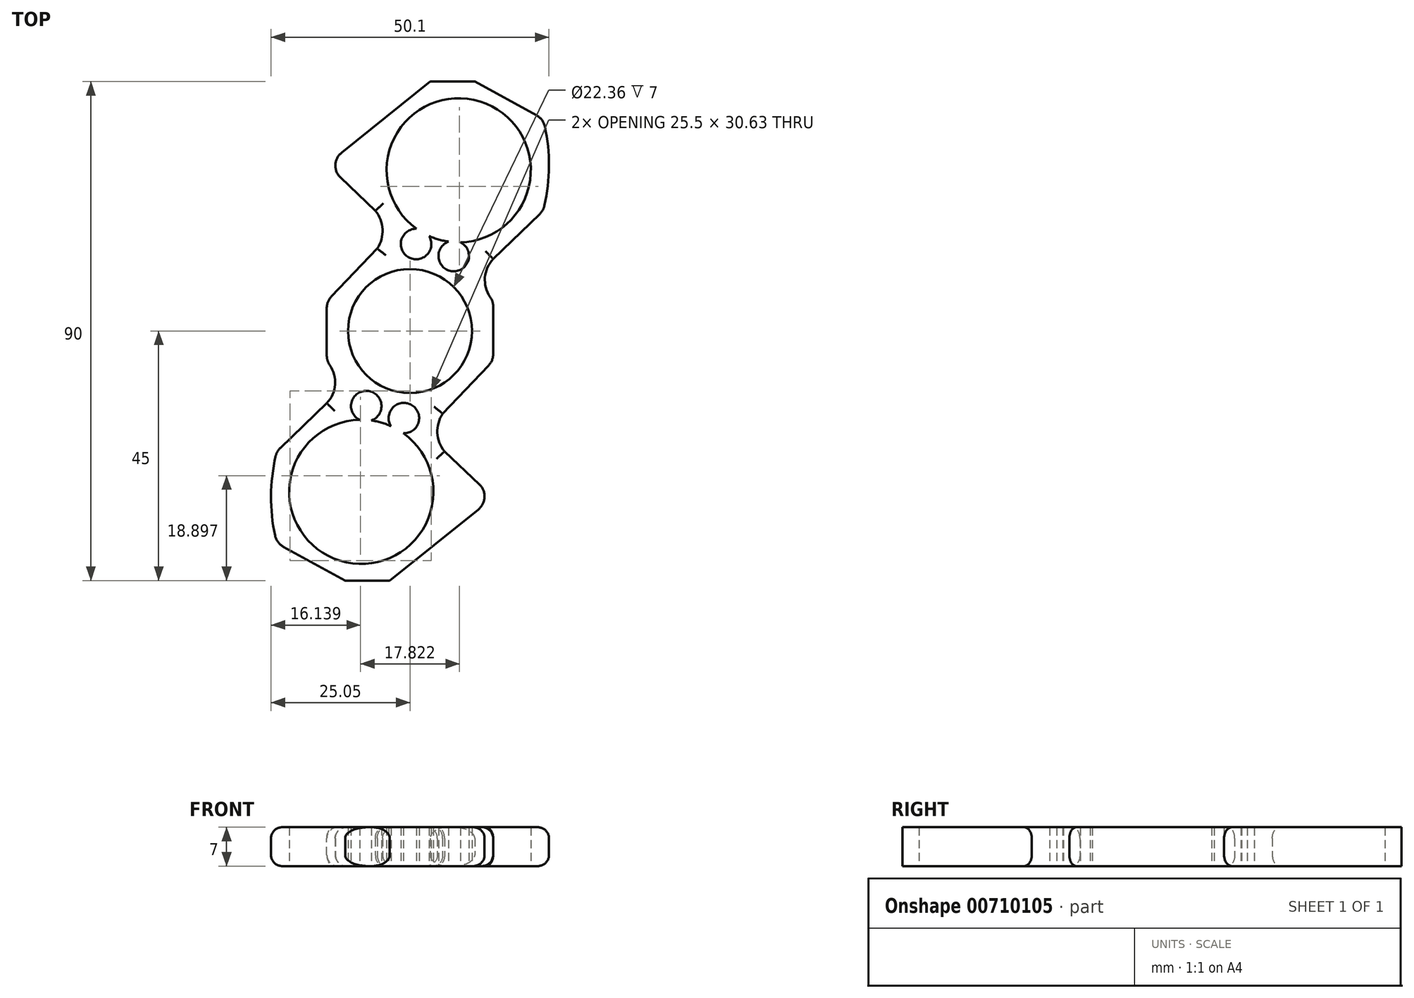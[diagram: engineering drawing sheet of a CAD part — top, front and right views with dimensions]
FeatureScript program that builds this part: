
annotation { "Feature Type Name" : "Feature", "Feature Type Description" : "" }
export const myFeature = defineFeature(function(context is Context, id is Id, definition is map)
    precondition{}
    {
        {
            var Q0;
            Q0=qCreatedBy(makeId("Top.planeOp"),FACE);
            var sketch = newSketch(context, id + "F0", { "sketchPlane" : qUnion([Q0])});
            skLineSegment(sketch, "E0.bottom", {"start": v(11.7, 45) * mm, "end": v(3.66, 45) * mm});
            skLineSegment(sketch, "E0.top", {"start": v(-3.66, -45) * mm, "end": v(-11.7, -45) * mm});
            skLineSegment(sketch, "E0.left", {"start": v(15, 43.2) * mm, "end": v(15, 13) * mm});
            skLineSegment(sketch, "E0.right", {"start": v(-15, 5.33) * mm, "end": v(-15, -43.2) * mm});
            skPoint(sketch, "E0.middle", {"position": v(0, 0) * mm});
            skCircle(sketch, "E1", {"center": v(0, 0) * mm, "radius": 11.18 * mm});
            skCircle(sketch, "E2", {"center": v(0, 0) * mm, "radius": 13 * mm});
            skLineSegment(sketch, "E3.right", {"start": v(24, 38.27) * mm, "end": v(24, 21.7) * mm});
            skLineSegment(sketch, "E4.left", {"start": v(-15, -45) * mm, "end": v(-15, -13) * mm});
            skLineSegment(sketch, "E4.right", {"start": v(-24, -38.27) * mm, "end": v(-24, -21.7) * mm});
            skPoint(sketch, "E5", {"position": v(-15, -29) * mm});
            skPoint(sketch, "E6", {"position": v(-8.78, -29) * mm});
            skCircle(sketch, "E7", {"center": v(-8.78, -29) * mm, "radius": 11.18 * mm});
            skCircle(sketch, "E8", {"center": v(-8.78, -29) * mm, "radius": 13 * mm});
            skCircle(sketch, "E9.1.0", {"center": v(8.78, 29) * mm, "radius": 11.18 * mm});
            skCircle(sketch, "E9.1.1", {"center": v(8.78, 29) * mm, "radius": 13 * mm});
            skLineSegment(sketch, "E10", {"start": v(-15, 5.33) * mm, "end": v(-5.35, 15.48) * mm});
            skLineSegment(sketch, "E11", {"start": v(-5.35, 15.48) * mm, "end": v(-2.67, 18.3) * mm});
            skLineSegment(sketch, "E12", {"start": v(-2.67, 18.3) * mm, "end": v(-15, 30.03) * mm});
            skLineSegment(sketch, "E13", {"start": v(-15, 30.03) * mm, "end": v(3.66, 45) * mm});
            skLineSegment(sketch, "E14", {"start": v(3.66, 45) * mm, "end": v(11.7, 45) * mm});
            skLineSegment(sketch, "E15", {"start": v(11.7, 45) * mm, "end": v(24, 38.27) * mm});
            skLineSegment(sketch, "E16", {"start": v(24, 21.7) * mm, "end": v(15, 13) * mm});
            skPoint(sketch, "E17.orphan", {"position": v(-15, 45) * mm});
            skPoint(sketch, "E18.orphan", {"position": v(24, 45) * mm});
            skPoint(sketch, "E19.orphan", {"position": v(15, 45) * mm});
            skPoint(sketch, "E20.orphan", {"position": v(24, 13) * mm});
            skLineSegment(sketch, "E21", {"start": v(15, 5.48) * mm, "end": v(10.3, 10.42) * mm});
            skLineSegment(sketch, "E22", {"start": v(10.3, 10.42) * mm, "end": v(15, 13) * mm});
            skLineSegment(sketch, "E23.trimOffspring", {"start": v(15, 5.48) * mm, "end": v(15, -5.33) * mm});
            skArc(sketch, "E24", {"start": v(11.7, 45) * mm, "mid": v(7.68, 46.41) * mm, "end": v(3.66, 45) * mm});
            skArc(sketch, "E25", {"start": v(24, 21.7) * mm, "mid": v(25.05, 29.98) * mm, "end": v(24, 38.27) * mm});
            skArc(sketch, "E26", {"start": v(-5.9, 14.9) * mm, "mid": v(-4.94, 18.35) * mm, "end": v(-6.24, 21.7) * mm});
            skArc(sketch, "E27", {"start": v(15, 13) * mm, "mid": v(13.5, 9.24) * mm, "end": v(15, 5.48) * mm});
            skLineSegment(sketch, "E28.1.0", {"start": v(15, -30.03) * mm, "end": v(-3.66, -45) * mm});
            skLineSegment(sketch, "E28.1.1", {"start": v(2.67, -18.3) * mm, "end": v(15, -30.03) * mm});
            skArc(sketch, "E28.1.2", {"start": v(5.9, -14.9) * mm, "mid": v(4.94, -18.35) * mm, "end": v(6.24, -21.7) * mm});
            skLineSegment(sketch, "E28.1.3", {"start": v(5.35, -15.48) * mm, "end": v(2.67, -18.3) * mm});
            skLineSegment(sketch, "E28.1.4", {"start": v(15, -5.33) * mm, "end": v(5.35, -15.48) * mm});
            skArc(sketch, "E28.1.5", {"start": v(-15, -13) * mm, "mid": v(-13.5, -9.24) * mm, "end": v(-15, -5.48) * mm});
            skLineSegment(sketch, "E28.1.6", {"start": v(-10.3, -10.42) * mm, "end": v(-15, -13) * mm});
            skLineSegment(sketch, "E28.1.7", {"start": v(-15, -5.48) * mm, "end": v(-10.3, -10.42) * mm});
            skLineSegment(sketch, "E28.1.8", {"start": v(-24, -21.7) * mm, "end": v(-15, -13) * mm});
            skArc(sketch, "E28.1.10", {"start": v(-24, -21.7) * mm, "mid": v(-25.05, -29.98) * mm, "end": v(-24, -38.27) * mm});
            skLineSegment(sketch, "E28.1.11", {"start": v(-11.7, -45) * mm, "end": v(-24, -38.27) * mm});
            skArc(sketch, "E28.1.13", {"start": v(-11.7, -45) * mm, "mid": v(-7.68, -46.41) * mm, "end": v(-3.66, -45) * mm});
            skPoint(sketch, "E29.orphan", {"position": v(-24, -13) * mm});
            skPoint(sketch, "E30.orphan", {"position": v(-24, -45) * mm});
            skPoint(sketch, "E31.orphan", {"position": v(15, -45) * mm});
            skSolve(sketch);
        }
        {
            var Q0;
            Q0=makeQuery(id+"F0.imprint","IMPRINT",FACE,{"disambiguationData":[TD([[makeQuery(id+"F0.imprint","IMPRINT",EDGE,{"derivedFrom":sQuery(id+"F0.wireOp",EDGE,"E2")}),-1.0]])]});
            var Q1;
            {var subQ0=sQuery(id+"F0.wireOp",EDGE,"E28.1.8");Q1=makeQuery(id+"F0.imprint","IMPRINT",FACE,{"disambiguationData":[TD([[makeQuery(id+"F0.imprint","IMPRINT",EDGE,{"derivedFrom":subQ0}),-1.0]])]});}
            var Q2;
            Q2=makeQuery(id+"F0.imprint","IMPRINT",FACE,{"disambiguationData":[TD([[makeQuery(id+"F0.imprint","IMPRINT",EDGE,{"derivedFrom":sQuery(id+"F0.wireOp",EDGE,"E4.right")}),1.0]])]});
            var Q3;
            Q3=makeQuery(id+"F0.imprint","IMPRINT",FACE,{"disambiguationData":[TD([[makeQuery(id+"F0.imprint","IMPRINT",EDGE,{"derivedFrom":sQuery(id+"F0.wireOp",EDGE,"E0.top")}),1.0]])]});
            var Q4;
            {var subQ0=sQuery(id+"F0.wireOp",EDGE,"E8");var subQ1=sQuery(id+"F0.wireOp",EDGE,"E4.left");var subQ2=makeQuery(id+"F0.imprint","INTERSECT",VERTEX,{"disambiguationData":[OD(0.0)],"derivedFrom":[subQ1,subQ0]});Q4=makeQuery(id+"F0.imprint","IMPRINT",FACE,{"disambiguationData":[TD([[makeQuery(id+"F0.imprint","IMPRINT",EDGE,{"disambiguationData":[TD([[subQ2,-1.0]])],"derivedFrom":subQ1}),-1.0]])]});}
            var Q5;
            {var subQ0=sQuery(id+"F0.wireOp",EDGE,"E8");var subQ1=sQuery(id+"F0.wireOp",EDGE,"E4.left");var subQ2=makeQuery(id+"F0.imprint","INTERSECT",VERTEX,{"disambiguationData":[OD(0.0)],"derivedFrom":[subQ1,subQ0]});Q5=makeQuery(id+"F0.imprint","IMPRINT",FACE,{"disambiguationData":[TD([[makeQuery(id+"F0.imprint","IMPRINT",EDGE,{"disambiguationData":[TD([[subQ2,-1.0]])],"derivedFrom":subQ1}),1.0]])]});}
            var Q6;
            Q6=makeQuery(id+"F0.imprint","IMPRINT",FACE,{"disambiguationData":[TD([[makeQuery(id+"F0.imprint","IMPRINT",EDGE,{"derivedFrom":sQuery(id+"F0.wireOp",EDGE,"E1")}),-1.0]])]});
            var Q7;
            {var subQ0=sQuery(id+"F0.wireOp",EDGE,"E9.1.1");var subQ1=sQuery(id+"F0.wireOp",EDGE,"E0.left");var subQ2=makeQuery(id+"F0.imprint","INTERSECT",VERTEX,{"disambiguationData":[OD(0.0)],"derivedFrom":[subQ1,subQ0]});Q7=makeQuery(id+"F0.imprint","IMPRINT",FACE,{"disambiguationData":[TD([[makeQuery(id+"F0.imprint","IMPRINT",EDGE,{"disambiguationData":[TD([[subQ2,-1.0]])],"derivedFrom":subQ1}),1.0]])]});}
            var Q8;
            {var subQ0=sQuery(id+"F0.wireOp",EDGE,"E9.1.1");var subQ1=sQuery(id+"F0.wireOp",EDGE,"E0.left");var subQ2=makeQuery(id+"F0.imprint","INTERSECT",VERTEX,{"disambiguationData":[OD(0.0)],"derivedFrom":[subQ1,subQ0]});Q8=makeQuery(id+"F0.imprint","IMPRINT",FACE,{"disambiguationData":[TD([[makeQuery(id+"F0.imprint","IMPRINT",EDGE,{"disambiguationData":[TD([[subQ2,-1.0]])],"derivedFrom":subQ1}),-1.0]])]});}
            var Q9;
            Q9=makeQuery(id+"F0.imprint","IMPRINT",FACE,{"disambiguationData":[TD([[makeQuery(id+"F0.imprint","IMPRINT",EDGE,{"derivedFrom":sQuery(id+"F0.wireOp",EDGE,"E3.right")}),1.0]])]});
            var Q10;
            {var subQ3=sQuery(id+"F0.wireOp",EDGE,"E3.right");Q10=makeQuery(id+"F0.imprint","IMPRINT",FACE,{"disambiguationData":[TD([[makeQuery(id+"F0.imprint","IMPRINT",EDGE,{"derivedFrom":subQ3}),-1.0]])]});}
            var Q11;
            Q11=makeQuery(id+"F0.imprint","IMPRINT",FACE,{"disambiguationData":[TD([[makeQuery(id+"F0.imprint","IMPRINT",EDGE,{"derivedFrom":sQuery(id+"F0.wireOp",EDGE,"E14")}),1.0]])]});
            var Q12;
            {var subQ2=sQuery(id+"F0.wireOp",EDGE,"E28.1.2");Q12=makeQuery(id+"F0.imprint","IMPRINT",FACE,{"disambiguationData":[TD([[makeQuery(id+"F0.imprint","IMPRINT",EDGE,{"derivedFrom":subQ2}),-1.0]])]});}
            var Q13;
            {var subQ0=sQuery(id+"F0.wireOp",EDGE,"E11");Q13=makeQuery(id+"F0.imprint","IMPRINT",FACE,{"disambiguationData":[TD([[makeQuery(id+"F0.imprint","IMPRINT",EDGE,{"derivedFrom":subQ0}),1.0]])]});}
            var Q14;
            Q14=makeQuery(id+"F0.imprint","IMPRINT",FACE,{"disambiguationData":[TD([[makeQuery(id+"F0.imprint","IMPRINT",EDGE,{"derivedFrom":sQuery(id+"F0.wireOp",EDGE,"E28.1.5")}),-1.0]])]});
            var Q15;
            Q15=makeQuery(id+"F0.imprint","IMPRINT",FACE,{"disambiguationData":[TD([[makeQuery(id+"F0.imprint","IMPRINT",EDGE,{"derivedFrom":sQuery(id+"F0.wireOp",EDGE,"E21")}),-1.0]])]});
            extrude(context, id + "F1", {"entities" : qUnion([Q0, Q1, Q2, Q3, Q4, Q5, Q6, Q7, Q8, Q9, Q10, Q11, Q12, Q13, Q14, Q15]), "depth" : 7 * mm, "offsetDistance" : 25 * mm});
        }
        {
            var Q0;
            Q0=makeQuery(id+"F1.opExtrude","SWEPT_EDGE",EDGE,{"disambiguationData":[OSD([sQuery(id+"F0.wireOp",EDGE,"E28.1.0"),sQuery(id+"F0.wireOp",EDGE,"E28.1.1")])]});
            var Q1;
            Q1=makeQuery(id+"F1.opExtrude","SWEPT_EDGE",EDGE,{"disambiguationData":[OSD([sQuery(id+"F0.wireOp",EDGE,"E12"),sQuery(id+"F0.wireOp",EDGE,"E13")])]});
            var Q2;
            Q2=makeQuery(id+"F1.opExtrude","SWEPT_EDGE",EDGE,{"disambiguationData":[OSD([sQuery(id+"F0.wireOp",EDGE,"E15"),sQuery(id+"F0.wireOp",EDGE,"E3.right"),sQuery(id+"F0.wireOp",EDGE,"E25")])]});
            var Q3;
            Q3=makeQuery(id+"F1.opExtrude","SWEPT_EDGE",EDGE,{"disambiguationData":[OSD([sQuery(id+"F0.wireOp",EDGE,"E3.right"),sQuery(id+"F0.wireOp",EDGE,"E16"),sQuery(id+"F0.wireOp",EDGE,"E25")])]});
            var Q4;
            Q4=makeQuery(id+"F1.opExtrude","SWEPT_EDGE",EDGE,{"disambiguationData":[OSD([sQuery(id+"F0.wireOp",EDGE,"E21"),sQuery(id+"F0.wireOp",EDGE,"E23.trimOffspring"),sQuery(id+"F0.wireOp",EDGE,"E27")])]});
            var Q5;
            Q5=makeQuery(id+"F1.opExtrude","SWEPT_EDGE",EDGE,{"disambiguationData":[OSD([sQuery(id+"F0.wireOp",EDGE,"E23.trimOffspring"),sQuery(id+"F0.wireOp",EDGE,"E28.1.4")])]});
            var Q6;
            Q6=makeQuery(id+"F1.opExtrude","SWEPT_EDGE",EDGE,{"disambiguationData":[OSD([sQuery(id+"F0.wireOp",EDGE,"E4.right"),sQuery(id+"F0.wireOp",EDGE,"E28.1.10"),sQuery(id+"F0.wireOp",EDGE,"E28.1.11")])]});
            var Q7;
            Q7=makeQuery(id+"F1.opExtrude","SWEPT_EDGE",EDGE,{"disambiguationData":[OSD([sQuery(id+"F0.wireOp",EDGE,"E28.1.8"),sQuery(id+"F0.wireOp",EDGE,"E4.right"),sQuery(id+"F0.wireOp",EDGE,"E28.1.10")])]});
            var Q8;
            Q8=makeQuery(id+"F1.opExtrude","SWEPT_EDGE",EDGE,{"disambiguationData":[OSD([sQuery(id+"F0.wireOp",EDGE,"E0.right"),sQuery(id+"F0.wireOp",EDGE,"E28.1.5"),sQuery(id+"F0.wireOp",EDGE,"E28.1.7")])]});
            var Q9;
            Q9=makeQuery(id+"F1.opExtrude","SWEPT_EDGE",EDGE,{"disambiguationData":[OSD([sQuery(id+"F0.wireOp",EDGE,"E0.right"),sQuery(id+"F0.wireOp",EDGE,"E10")])]});
            fillet(context, id + "F2", {"entities" : qUnion([Q0, Q1, Q2, Q3, Q4, Q5, Q6, Q7, Q8, Q9]), "radius" : 3 * mm, "tangentPropagation" : true, "allowEdgeOverflow" : false});
        }
        {
            var Q0;
            Q0=makeQuery(id+"F1.opExtrude","CAP_EDGE",EDGE,{"disambiguationData":[OSD([sQuery(id+"F0.wireOp",EDGE,"E23.trimOffspring")])],"isStart":true});
            var Q1;
            {var subQ0=sQuery(id+"F0.wireOp",EDGE,"E28.1.4");var subQ1=sQuery(id+"F0.wireOp",EDGE,"E23.trimOffspring");Q1=makeQuery(id+"F2.opFillet","BLEND_EDGE",EDGE,{"blendedFrom":[makeQuery(id+"F1.opExtrude","SWEPT_EDGE",EDGE,{"disambiguationData":[OSD([subQ1,subQ0])]}),makeQuery(id+"F1.opExtrude","CAP_FACE",FACE,{"disambiguationData":[OSD([sQuery(id+"F0.wireOp",EDGE,"E0.right"),sQuery(id+"F0.wireOp",EDGE,"E1"),sQuery(id+"F0.wireOp",EDGE,"E7"),sQuery(id+"F0.wireOp",EDGE,"E9.1.0"),sQuery(id+"F0.wireOp",EDGE,"E10"),sQuery(id+"F0.wireOp",EDGE,"E12"),sQuery(id+"F0.wireOp",EDGE,"E13"),sQuery(id+"F0.wireOp",EDGE,"E15"),sQuery(id+"F0.wireOp",EDGE,"E16"),subQ1,sQuery(id+"F0.wireOp",EDGE,"E24"),sQuery(id+"F0.wireOp",EDGE,"E25"),sQuery(id+"F0.wireOp",EDGE,"E26"),sQuery(id+"F0.wireOp",EDGE,"E27"),sQuery(id+"F0.wireOp",EDGE,"E28.1.0"),sQuery(id+"F0.wireOp",EDGE,"E28.1.1"),sQuery(id+"F0.wireOp",EDGE,"E28.1.2"),subQ0,sQuery(id+"F0.wireOp",EDGE,"E28.1.5"),sQuery(id+"F0.wireOp",EDGE,"E28.1.8"),sQuery(id+"F0.wireOp",EDGE,"E28.1.10"),sQuery(id+"F0.wireOp",EDGE,"E28.1.11"),sQuery(id+"F0.wireOp",EDGE,"E28.1.13")])],"isStart":true})],"blendedInto":[makeQuery(id+"F1.opExtrude","CAP_FACE",FACE,{"disambiguationData":[OSD([sQuery(id+"F0.wireOp",EDGE,"E0.right"),sQuery(id+"F0.wireOp",EDGE,"E1"),sQuery(id+"F0.wireOp",EDGE,"E7"),sQuery(id+"F0.wireOp",EDGE,"E9.1.0"),sQuery(id+"F0.wireOp",EDGE,"E10"),sQuery(id+"F0.wireOp",EDGE,"E12"),sQuery(id+"F0.wireOp",EDGE,"E13"),sQuery(id+"F0.wireOp",EDGE,"E15"),sQuery(id+"F0.wireOp",EDGE,"E16"),subQ1,sQuery(id+"F0.wireOp",EDGE,"E24"),sQuery(id+"F0.wireOp",EDGE,"E25"),sQuery(id+"F0.wireOp",EDGE,"E26"),sQuery(id+"F0.wireOp",EDGE,"E27"),sQuery(id+"F0.wireOp",EDGE,"E28.1.0"),sQuery(id+"F0.wireOp",EDGE,"E28.1.1"),sQuery(id+"F0.wireOp",EDGE,"E28.1.2"),subQ0,sQuery(id+"F0.wireOp",EDGE,"E28.1.5"),sQuery(id+"F0.wireOp",EDGE,"E28.1.8"),sQuery(id+"F0.wireOp",EDGE,"E28.1.10"),sQuery(id+"F0.wireOp",EDGE,"E28.1.11"),sQuery(id+"F0.wireOp",EDGE,"E28.1.13")])],"isStart":true})]});}
            var Q2;
            Q2=makeQuery(id+"F1.opExtrude","CAP_EDGE",EDGE,{"disambiguationData":[OSD([sQuery(id+"F0.wireOp",EDGE,"E28.1.4")])],"isStart":true});
            var Q3;
            Q3=makeQuery(id+"F1.opExtrude","CAP_EDGE",EDGE,{"disambiguationData":[OSD([sQuery(id+"F0.wireOp",EDGE,"E28.1.2")])],"isStart":true});
            var Q4;
            Q4=makeQuery(id+"F1.opExtrude","CAP_EDGE",EDGE,{"disambiguationData":[OSD([sQuery(id+"F0.wireOp",EDGE,"E28.1.1")])],"isStart":true});
            var Q5;
            {var subQ0=sQuery(id+"F0.wireOp",EDGE,"E28.1.1");var subQ1=sQuery(id+"F0.wireOp",EDGE,"E28.1.0");Q5=makeQuery(id+"F2.opFillet","BLEND_EDGE",EDGE,{"blendedFrom":[makeQuery(id+"F1.opExtrude","SWEPT_EDGE",EDGE,{"disambiguationData":[OSD([subQ1,subQ0])]}),makeQuery(id+"F1.opExtrude","CAP_FACE",FACE,{"disambiguationData":[OSD([sQuery(id+"F0.wireOp",EDGE,"E0.right"),sQuery(id+"F0.wireOp",EDGE,"E1"),sQuery(id+"F0.wireOp",EDGE,"E7"),sQuery(id+"F0.wireOp",EDGE,"E9.1.0"),sQuery(id+"F0.wireOp",EDGE,"E10"),sQuery(id+"F0.wireOp",EDGE,"E12"),sQuery(id+"F0.wireOp",EDGE,"E13"),sQuery(id+"F0.wireOp",EDGE,"E15"),sQuery(id+"F0.wireOp",EDGE,"E16"),sQuery(id+"F0.wireOp",EDGE,"E23.trimOffspring"),sQuery(id+"F0.wireOp",EDGE,"E24"),sQuery(id+"F0.wireOp",EDGE,"E25"),sQuery(id+"F0.wireOp",EDGE,"E26"),sQuery(id+"F0.wireOp",EDGE,"E27"),subQ1,subQ0,sQuery(id+"F0.wireOp",EDGE,"E28.1.2"),sQuery(id+"F0.wireOp",EDGE,"E28.1.4"),sQuery(id+"F0.wireOp",EDGE,"E28.1.5"),sQuery(id+"F0.wireOp",EDGE,"E28.1.8"),sQuery(id+"F0.wireOp",EDGE,"E28.1.10"),sQuery(id+"F0.wireOp",EDGE,"E28.1.11"),sQuery(id+"F0.wireOp",EDGE,"E28.1.13")])],"isStart":true})],"blendedInto":[makeQuery(id+"F1.opExtrude","CAP_FACE",FACE,{"disambiguationData":[OSD([sQuery(id+"F0.wireOp",EDGE,"E0.right"),sQuery(id+"F0.wireOp",EDGE,"E1"),sQuery(id+"F0.wireOp",EDGE,"E7"),sQuery(id+"F0.wireOp",EDGE,"E9.1.0"),sQuery(id+"F0.wireOp",EDGE,"E10"),sQuery(id+"F0.wireOp",EDGE,"E12"),sQuery(id+"F0.wireOp",EDGE,"E13"),sQuery(id+"F0.wireOp",EDGE,"E15"),sQuery(id+"F0.wireOp",EDGE,"E16"),sQuery(id+"F0.wireOp",EDGE,"E23.trimOffspring"),sQuery(id+"F0.wireOp",EDGE,"E24"),sQuery(id+"F0.wireOp",EDGE,"E25"),sQuery(id+"F0.wireOp",EDGE,"E26"),sQuery(id+"F0.wireOp",EDGE,"E27"),subQ1,subQ0,sQuery(id+"F0.wireOp",EDGE,"E28.1.2"),sQuery(id+"F0.wireOp",EDGE,"E28.1.4"),sQuery(id+"F0.wireOp",EDGE,"E28.1.5"),sQuery(id+"F0.wireOp",EDGE,"E28.1.8"),sQuery(id+"F0.wireOp",EDGE,"E28.1.10"),sQuery(id+"F0.wireOp",EDGE,"E28.1.11"),sQuery(id+"F0.wireOp",EDGE,"E28.1.13")])],"isStart":true})]});}
            var Q6;
            Q6=makeQuery(id+"F1.opExtrude","CAP_EDGE",EDGE,{"disambiguationData":[OSD([sQuery(id+"F0.wireOp",EDGE,"E28.1.0")])],"isStart":true});
            var Q7;
            Q7=makeQuery(id+"F1.opExtrude","CAP_EDGE",EDGE,{"disambiguationData":[OSD([sQuery(id+"F0.wireOp",EDGE,"E28.1.13")])],"isStart":true});
            var Q8;
            Q8=makeQuery(id+"F1.opExtrude","CAP_EDGE",EDGE,{"disambiguationData":[OSD([sQuery(id+"F0.wireOp",EDGE,"E28.1.11")])],"isStart":true});
            var Q9;
            Q9=makeQuery(id+"F1.opExtrude","CAP_EDGE",EDGE,{"disambiguationData":[OSD([sQuery(id+"F0.wireOp",EDGE,"E0.right")])],"isStart":true});
            var Q10;
            {var subQ0=sQuery(id+"F0.wireOp",EDGE,"E10");var subQ1=sQuery(id+"F0.wireOp",EDGE,"E0.right");Q10=makeQuery(id+"F2.opFillet","BLEND_EDGE",EDGE,{"blendedFrom":[makeQuery(id+"F1.opExtrude","SWEPT_EDGE",EDGE,{"disambiguationData":[OSD([subQ1,subQ0])]}),makeQuery(id+"F1.opExtrude","CAP_FACE",FACE,{"disambiguationData":[OSD([subQ1,sQuery(id+"F0.wireOp",EDGE,"E1"),sQuery(id+"F0.wireOp",EDGE,"E7"),sQuery(id+"F0.wireOp",EDGE,"E9.1.0"),subQ0,sQuery(id+"F0.wireOp",EDGE,"E12"),sQuery(id+"F0.wireOp",EDGE,"E13"),sQuery(id+"F0.wireOp",EDGE,"E15"),sQuery(id+"F0.wireOp",EDGE,"E16"),sQuery(id+"F0.wireOp",EDGE,"E23.trimOffspring"),sQuery(id+"F0.wireOp",EDGE,"E24"),sQuery(id+"F0.wireOp",EDGE,"E25"),sQuery(id+"F0.wireOp",EDGE,"E26"),sQuery(id+"F0.wireOp",EDGE,"E27"),sQuery(id+"F0.wireOp",EDGE,"E28.1.0"),sQuery(id+"F0.wireOp",EDGE,"E28.1.1"),sQuery(id+"F0.wireOp",EDGE,"E28.1.2"),sQuery(id+"F0.wireOp",EDGE,"E28.1.4"),sQuery(id+"F0.wireOp",EDGE,"E28.1.5"),sQuery(id+"F0.wireOp",EDGE,"E28.1.8"),sQuery(id+"F0.wireOp",EDGE,"E28.1.10"),sQuery(id+"F0.wireOp",EDGE,"E28.1.11"),sQuery(id+"F0.wireOp",EDGE,"E28.1.13")])],"isStart":true})],"blendedInto":[makeQuery(id+"F1.opExtrude","CAP_FACE",FACE,{"disambiguationData":[OSD([subQ1,sQuery(id+"F0.wireOp",EDGE,"E1"),sQuery(id+"F0.wireOp",EDGE,"E7"),sQuery(id+"F0.wireOp",EDGE,"E9.1.0"),subQ0,sQuery(id+"F0.wireOp",EDGE,"E12"),sQuery(id+"F0.wireOp",EDGE,"E13"),sQuery(id+"F0.wireOp",EDGE,"E15"),sQuery(id+"F0.wireOp",EDGE,"E16"),sQuery(id+"F0.wireOp",EDGE,"E23.trimOffspring"),sQuery(id+"F0.wireOp",EDGE,"E24"),sQuery(id+"F0.wireOp",EDGE,"E25"),sQuery(id+"F0.wireOp",EDGE,"E26"),sQuery(id+"F0.wireOp",EDGE,"E27"),sQuery(id+"F0.wireOp",EDGE,"E28.1.0"),sQuery(id+"F0.wireOp",EDGE,"E28.1.1"),sQuery(id+"F0.wireOp",EDGE,"E28.1.2"),sQuery(id+"F0.wireOp",EDGE,"E28.1.4"),sQuery(id+"F0.wireOp",EDGE,"E28.1.5"),sQuery(id+"F0.wireOp",EDGE,"E28.1.8"),sQuery(id+"F0.wireOp",EDGE,"E28.1.10"),sQuery(id+"F0.wireOp",EDGE,"E28.1.11"),sQuery(id+"F0.wireOp",EDGE,"E28.1.13")])],"isStart":true})]});}
            var Q11;
            Q11=makeQuery(id+"F1.opExtrude","CAP_EDGE",EDGE,{"disambiguationData":[OSD([sQuery(id+"F0.wireOp",EDGE,"E26")])],"isStart":true});
            var Q12;
            Q12=makeQuery(id+"F1.opExtrude","CAP_EDGE",EDGE,{"disambiguationData":[OSD([sQuery(id+"F0.wireOp",EDGE,"E12")])],"isStart":true});
            var Q13;
            Q13=makeQuery(id+"F1.opExtrude","CAP_EDGE",EDGE,{"disambiguationData":[OSD([sQuery(id+"F0.wireOp",EDGE,"E13")])],"isStart":true});
            var Q14;
            {var subQ0=sQuery(id+"F0.wireOp",EDGE,"E13");var subQ1=sQuery(id+"F0.wireOp",EDGE,"E12");Q14=makeQuery(id+"F2.opFillet","BLEND_EDGE",EDGE,{"blendedFrom":[makeQuery(id+"F1.opExtrude","SWEPT_EDGE",EDGE,{"disambiguationData":[OSD([subQ1,subQ0])]}),makeQuery(id+"F1.opExtrude","CAP_FACE",FACE,{"disambiguationData":[OSD([sQuery(id+"F0.wireOp",EDGE,"E0.right"),sQuery(id+"F0.wireOp",EDGE,"E1"),sQuery(id+"F0.wireOp",EDGE,"E7"),sQuery(id+"F0.wireOp",EDGE,"E9.1.0"),sQuery(id+"F0.wireOp",EDGE,"E10"),subQ1,subQ0,sQuery(id+"F0.wireOp",EDGE,"E15"),sQuery(id+"F0.wireOp",EDGE,"E16"),sQuery(id+"F0.wireOp",EDGE,"E23.trimOffspring"),sQuery(id+"F0.wireOp",EDGE,"E24"),sQuery(id+"F0.wireOp",EDGE,"E25"),sQuery(id+"F0.wireOp",EDGE,"E26"),sQuery(id+"F0.wireOp",EDGE,"E27"),sQuery(id+"F0.wireOp",EDGE,"E28.1.0"),sQuery(id+"F0.wireOp",EDGE,"E28.1.1"),sQuery(id+"F0.wireOp",EDGE,"E28.1.2"),sQuery(id+"F0.wireOp",EDGE,"E28.1.4"),sQuery(id+"F0.wireOp",EDGE,"E28.1.5"),sQuery(id+"F0.wireOp",EDGE,"E28.1.8"),sQuery(id+"F0.wireOp",EDGE,"E28.1.10"),sQuery(id+"F0.wireOp",EDGE,"E28.1.11"),sQuery(id+"F0.wireOp",EDGE,"E28.1.13")])],"isStart":true})],"blendedInto":[makeQuery(id+"F1.opExtrude","CAP_FACE",FACE,{"disambiguationData":[OSD([sQuery(id+"F0.wireOp",EDGE,"E0.right"),sQuery(id+"F0.wireOp",EDGE,"E1"),sQuery(id+"F0.wireOp",EDGE,"E7"),sQuery(id+"F0.wireOp",EDGE,"E9.1.0"),sQuery(id+"F0.wireOp",EDGE,"E10"),subQ1,subQ0,sQuery(id+"F0.wireOp",EDGE,"E15"),sQuery(id+"F0.wireOp",EDGE,"E16"),sQuery(id+"F0.wireOp",EDGE,"E23.trimOffspring"),sQuery(id+"F0.wireOp",EDGE,"E24"),sQuery(id+"F0.wireOp",EDGE,"E25"),sQuery(id+"F0.wireOp",EDGE,"E26"),sQuery(id+"F0.wireOp",EDGE,"E27"),sQuery(id+"F0.wireOp",EDGE,"E28.1.0"),sQuery(id+"F0.wireOp",EDGE,"E28.1.1"),sQuery(id+"F0.wireOp",EDGE,"E28.1.2"),sQuery(id+"F0.wireOp",EDGE,"E28.1.4"),sQuery(id+"F0.wireOp",EDGE,"E28.1.5"),sQuery(id+"F0.wireOp",EDGE,"E28.1.8"),sQuery(id+"F0.wireOp",EDGE,"E28.1.10"),sQuery(id+"F0.wireOp",EDGE,"E28.1.11"),sQuery(id+"F0.wireOp",EDGE,"E28.1.13")])],"isStart":true})]});}
            var Q15;
            Q15=makeQuery(id+"F1.opExtrude","CAP_EDGE",EDGE,{"disambiguationData":[OSD([sQuery(id+"F0.wireOp",EDGE,"E15")])],"isStart":true});
            fillet(context, id + "F3", {"entities" : qUnion([Q0, Q1, Q2, Q3, Q4, Q5, Q6, Q7, Q8, Q9, Q10, Q11, Q12, Q13, Q14, Q15]), "radius" : 2 * mm, "tangentPropagation" : true, "allowEdgeOverflow" : false});
        }
        {
            var Q0;
            Q0=makeQuery(id+"F1.opExtrude","CAP_EDGE",EDGE,{"disambiguationData":[OSD([sQuery(id+"F0.wireOp",EDGE,"E13")])],"isStart":false});
            var Q1;
            Q1=makeQuery(id+"F1.opExtrude","CAP_EDGE",EDGE,{"disambiguationData":[OSD([sQuery(id+"F0.wireOp",EDGE,"E10")])],"isStart":false});
            var Q2;
            Q2=makeQuery(id+"F1.opExtrude","CAP_EDGE",EDGE,{"disambiguationData":[OSD([sQuery(id+"F0.wireOp",EDGE,"E26")])],"isStart":false});
            var Q3;
            {var subQ0=sQuery(id+"F0.wireOp",EDGE,"E13");var subQ1=sQuery(id+"F0.wireOp",EDGE,"E12");Q3=makeQuery(id+"F2.opFillet","BLEND_EDGE",EDGE,{"blendedFrom":[makeQuery(id+"F1.opExtrude","SWEPT_EDGE",EDGE,{"disambiguationData":[OSD([subQ1,subQ0])]}),makeQuery(id+"F1.opExtrude","CAP_FACE",FACE,{"disambiguationData":[OSD([sQuery(id+"F0.wireOp",EDGE,"E0.right"),sQuery(id+"F0.wireOp",EDGE,"E1"),sQuery(id+"F0.wireOp",EDGE,"E7"),sQuery(id+"F0.wireOp",EDGE,"E9.1.0"),sQuery(id+"F0.wireOp",EDGE,"E10"),subQ1,subQ0,sQuery(id+"F0.wireOp",EDGE,"E15"),sQuery(id+"F0.wireOp",EDGE,"E16"),sQuery(id+"F0.wireOp",EDGE,"E23.trimOffspring"),sQuery(id+"F0.wireOp",EDGE,"E24"),sQuery(id+"F0.wireOp",EDGE,"E25"),sQuery(id+"F0.wireOp",EDGE,"E26"),sQuery(id+"F0.wireOp",EDGE,"E27"),sQuery(id+"F0.wireOp",EDGE,"E28.1.0"),sQuery(id+"F0.wireOp",EDGE,"E28.1.1"),sQuery(id+"F0.wireOp",EDGE,"E28.1.2"),sQuery(id+"F0.wireOp",EDGE,"E28.1.4"),sQuery(id+"F0.wireOp",EDGE,"E28.1.5"),sQuery(id+"F0.wireOp",EDGE,"E28.1.8"),sQuery(id+"F0.wireOp",EDGE,"E28.1.10"),sQuery(id+"F0.wireOp",EDGE,"E28.1.11"),sQuery(id+"F0.wireOp",EDGE,"E28.1.13")])],"isStart":false})],"blendedInto":[makeQuery(id+"F1.opExtrude","CAP_FACE",FACE,{"disambiguationData":[OSD([sQuery(id+"F0.wireOp",EDGE,"E0.right"),sQuery(id+"F0.wireOp",EDGE,"E1"),sQuery(id+"F0.wireOp",EDGE,"E7"),sQuery(id+"F0.wireOp",EDGE,"E9.1.0"),sQuery(id+"F0.wireOp",EDGE,"E10"),subQ1,subQ0,sQuery(id+"F0.wireOp",EDGE,"E15"),sQuery(id+"F0.wireOp",EDGE,"E16"),sQuery(id+"F0.wireOp",EDGE,"E23.trimOffspring"),sQuery(id+"F0.wireOp",EDGE,"E24"),sQuery(id+"F0.wireOp",EDGE,"E25"),sQuery(id+"F0.wireOp",EDGE,"E26"),sQuery(id+"F0.wireOp",EDGE,"E27"),sQuery(id+"F0.wireOp",EDGE,"E28.1.0"),sQuery(id+"F0.wireOp",EDGE,"E28.1.1"),sQuery(id+"F0.wireOp",EDGE,"E28.1.2"),sQuery(id+"F0.wireOp",EDGE,"E28.1.4"),sQuery(id+"F0.wireOp",EDGE,"E28.1.5"),sQuery(id+"F0.wireOp",EDGE,"E28.1.8"),sQuery(id+"F0.wireOp",EDGE,"E28.1.10"),sQuery(id+"F0.wireOp",EDGE,"E28.1.11"),sQuery(id+"F0.wireOp",EDGE,"E28.1.13")])],"isStart":false})]});}
            var Q4;
            Q4=makeQuery(id+"F1.opExtrude","CAP_EDGE",EDGE,{"disambiguationData":[OSD([sQuery(id+"F0.wireOp",EDGE,"E0.right")])],"isStart":false});
            var Q5;
            {var subQ0=sQuery(id+"F0.wireOp",EDGE,"E10");var subQ1=sQuery(id+"F0.wireOp",EDGE,"E0.right");Q5=makeQuery(id+"F2.opFillet","BLEND_EDGE",EDGE,{"blendedFrom":[makeQuery(id+"F1.opExtrude","SWEPT_EDGE",EDGE,{"disambiguationData":[OSD([subQ1,subQ0])]}),makeQuery(id+"F1.opExtrude","CAP_FACE",FACE,{"disambiguationData":[OSD([subQ1,sQuery(id+"F0.wireOp",EDGE,"E1"),sQuery(id+"F0.wireOp",EDGE,"E7"),sQuery(id+"F0.wireOp",EDGE,"E9.1.0"),subQ0,sQuery(id+"F0.wireOp",EDGE,"E12"),sQuery(id+"F0.wireOp",EDGE,"E13"),sQuery(id+"F0.wireOp",EDGE,"E15"),sQuery(id+"F0.wireOp",EDGE,"E16"),sQuery(id+"F0.wireOp",EDGE,"E23.trimOffspring"),sQuery(id+"F0.wireOp",EDGE,"E24"),sQuery(id+"F0.wireOp",EDGE,"E25"),sQuery(id+"F0.wireOp",EDGE,"E26"),sQuery(id+"F0.wireOp",EDGE,"E27"),sQuery(id+"F0.wireOp",EDGE,"E28.1.0"),sQuery(id+"F0.wireOp",EDGE,"E28.1.1"),sQuery(id+"F0.wireOp",EDGE,"E28.1.2"),sQuery(id+"F0.wireOp",EDGE,"E28.1.4"),sQuery(id+"F0.wireOp",EDGE,"E28.1.5"),sQuery(id+"F0.wireOp",EDGE,"E28.1.8"),sQuery(id+"F0.wireOp",EDGE,"E28.1.10"),sQuery(id+"F0.wireOp",EDGE,"E28.1.11"),sQuery(id+"F0.wireOp",EDGE,"E28.1.13")])],"isStart":false})],"blendedInto":[makeQuery(id+"F1.opExtrude","CAP_FACE",FACE,{"disambiguationData":[OSD([subQ1,sQuery(id+"F0.wireOp",EDGE,"E1"),sQuery(id+"F0.wireOp",EDGE,"E7"),sQuery(id+"F0.wireOp",EDGE,"E9.1.0"),subQ0,sQuery(id+"F0.wireOp",EDGE,"E12"),sQuery(id+"F0.wireOp",EDGE,"E13"),sQuery(id+"F0.wireOp",EDGE,"E15"),sQuery(id+"F0.wireOp",EDGE,"E16"),sQuery(id+"F0.wireOp",EDGE,"E23.trimOffspring"),sQuery(id+"F0.wireOp",EDGE,"E24"),sQuery(id+"F0.wireOp",EDGE,"E25"),sQuery(id+"F0.wireOp",EDGE,"E26"),sQuery(id+"F0.wireOp",EDGE,"E27"),sQuery(id+"F0.wireOp",EDGE,"E28.1.0"),sQuery(id+"F0.wireOp",EDGE,"E28.1.1"),sQuery(id+"F0.wireOp",EDGE,"E28.1.2"),sQuery(id+"F0.wireOp",EDGE,"E28.1.4"),sQuery(id+"F0.wireOp",EDGE,"E28.1.5"),sQuery(id+"F0.wireOp",EDGE,"E28.1.8"),sQuery(id+"F0.wireOp",EDGE,"E28.1.10"),sQuery(id+"F0.wireOp",EDGE,"E28.1.11"),sQuery(id+"F0.wireOp",EDGE,"E28.1.13")])],"isStart":false})]});}
            var Q6;
            Q6=makeQuery(id+"F1.opExtrude","CAP_EDGE",EDGE,{"disambiguationData":[OSD([sQuery(id+"F0.wireOp",EDGE,"E12")])],"isStart":false});
            var Q7;
            {var subQ0=sQuery(id+"F0.wireOp",EDGE,"E28.1.5");var subQ1=sQuery(id+"F0.wireOp",EDGE,"E0.right");Q7=makeQuery(id+"F2.opFillet","BLEND_EDGE",EDGE,{"blendedFrom":[makeQuery(id+"F1.opExtrude","SWEPT_EDGE",EDGE,{"disambiguationData":[OSD([subQ1,subQ0,sQuery(id+"F0.wireOp",EDGE,"E28.1.7")])]}),makeQuery(id+"F1.opExtrude","CAP_FACE",FACE,{"disambiguationData":[OSD([subQ1,sQuery(id+"F0.wireOp",EDGE,"E1"),sQuery(id+"F0.wireOp",EDGE,"E7"),sQuery(id+"F0.wireOp",EDGE,"E9.1.0"),sQuery(id+"F0.wireOp",EDGE,"E10"),sQuery(id+"F0.wireOp",EDGE,"E12"),sQuery(id+"F0.wireOp",EDGE,"E13"),sQuery(id+"F0.wireOp",EDGE,"E15"),sQuery(id+"F0.wireOp",EDGE,"E16"),sQuery(id+"F0.wireOp",EDGE,"E23.trimOffspring"),sQuery(id+"F0.wireOp",EDGE,"E24"),sQuery(id+"F0.wireOp",EDGE,"E25"),sQuery(id+"F0.wireOp",EDGE,"E26"),sQuery(id+"F0.wireOp",EDGE,"E27"),sQuery(id+"F0.wireOp",EDGE,"E28.1.0"),sQuery(id+"F0.wireOp",EDGE,"E28.1.1"),sQuery(id+"F0.wireOp",EDGE,"E28.1.2"),sQuery(id+"F0.wireOp",EDGE,"E28.1.4"),subQ0,sQuery(id+"F0.wireOp",EDGE,"E28.1.8"),sQuery(id+"F0.wireOp",EDGE,"E28.1.10"),sQuery(id+"F0.wireOp",EDGE,"E28.1.11"),sQuery(id+"F0.wireOp",EDGE,"E28.1.13")])],"isStart":false})],"blendedInto":[makeQuery(id+"F1.opExtrude","CAP_FACE",FACE,{"disambiguationData":[OSD([subQ1,sQuery(id+"F0.wireOp",EDGE,"E1"),sQuery(id+"F0.wireOp",EDGE,"E7"),sQuery(id+"F0.wireOp",EDGE,"E9.1.0"),sQuery(id+"F0.wireOp",EDGE,"E10"),sQuery(id+"F0.wireOp",EDGE,"E12"),sQuery(id+"F0.wireOp",EDGE,"E13"),sQuery(id+"F0.wireOp",EDGE,"E15"),sQuery(id+"F0.wireOp",EDGE,"E16"),sQuery(id+"F0.wireOp",EDGE,"E23.trimOffspring"),sQuery(id+"F0.wireOp",EDGE,"E24"),sQuery(id+"F0.wireOp",EDGE,"E25"),sQuery(id+"F0.wireOp",EDGE,"E26"),sQuery(id+"F0.wireOp",EDGE,"E27"),sQuery(id+"F0.wireOp",EDGE,"E28.1.0"),sQuery(id+"F0.wireOp",EDGE,"E28.1.1"),sQuery(id+"F0.wireOp",EDGE,"E28.1.2"),sQuery(id+"F0.wireOp",EDGE,"E28.1.4"),subQ0,sQuery(id+"F0.wireOp",EDGE,"E28.1.8"),sQuery(id+"F0.wireOp",EDGE,"E28.1.10"),sQuery(id+"F0.wireOp",EDGE,"E28.1.11"),sQuery(id+"F0.wireOp",EDGE,"E28.1.13")])],"isStart":false})]});}
            var Q8;
            Q8=makeQuery(id+"F1.opExtrude","CAP_EDGE",EDGE,{"disambiguationData":[OSD([sQuery(id+"F0.wireOp",EDGE,"E28.1.5")])],"isStart":false});
            var Q9;
            Q9=makeQuery(id+"F1.opExtrude","CAP_EDGE",EDGE,{"disambiguationData":[OSD([sQuery(id+"F0.wireOp",EDGE,"E28.1.8")])],"isStart":false});
            var Q10;
            {var subQ0=sQuery(id+"F0.wireOp",EDGE,"E28.1.10");var subQ1=sQuery(id+"F0.wireOp",EDGE,"E28.1.8");Q10=makeQuery(id+"F2.opFillet","BLEND_EDGE",EDGE,{"blendedFrom":[makeQuery(id+"F1.opExtrude","SWEPT_EDGE",EDGE,{"disambiguationData":[OSD([subQ1,sQuery(id+"F0.wireOp",EDGE,"E4.right"),subQ0])]}),makeQuery(id+"F1.opExtrude","CAP_FACE",FACE,{"disambiguationData":[OSD([sQuery(id+"F0.wireOp",EDGE,"E0.right"),sQuery(id+"F0.wireOp",EDGE,"E1"),sQuery(id+"F0.wireOp",EDGE,"E7"),sQuery(id+"F0.wireOp",EDGE,"E9.1.0"),sQuery(id+"F0.wireOp",EDGE,"E10"),sQuery(id+"F0.wireOp",EDGE,"E12"),sQuery(id+"F0.wireOp",EDGE,"E13"),sQuery(id+"F0.wireOp",EDGE,"E15"),sQuery(id+"F0.wireOp",EDGE,"E16"),sQuery(id+"F0.wireOp",EDGE,"E23.trimOffspring"),sQuery(id+"F0.wireOp",EDGE,"E24"),sQuery(id+"F0.wireOp",EDGE,"E25"),sQuery(id+"F0.wireOp",EDGE,"E26"),sQuery(id+"F0.wireOp",EDGE,"E27"),sQuery(id+"F0.wireOp",EDGE,"E28.1.0"),sQuery(id+"F0.wireOp",EDGE,"E28.1.1"),sQuery(id+"F0.wireOp",EDGE,"E28.1.2"),sQuery(id+"F0.wireOp",EDGE,"E28.1.4"),sQuery(id+"F0.wireOp",EDGE,"E28.1.5"),subQ1,subQ0,sQuery(id+"F0.wireOp",EDGE,"E28.1.11"),sQuery(id+"F0.wireOp",EDGE,"E28.1.13")])],"isStart":false})],"blendedInto":[makeQuery(id+"F1.opExtrude","CAP_FACE",FACE,{"disambiguationData":[OSD([sQuery(id+"F0.wireOp",EDGE,"E0.right"),sQuery(id+"F0.wireOp",EDGE,"E1"),sQuery(id+"F0.wireOp",EDGE,"E7"),sQuery(id+"F0.wireOp",EDGE,"E9.1.0"),sQuery(id+"F0.wireOp",EDGE,"E10"),sQuery(id+"F0.wireOp",EDGE,"E12"),sQuery(id+"F0.wireOp",EDGE,"E13"),sQuery(id+"F0.wireOp",EDGE,"E15"),sQuery(id+"F0.wireOp",EDGE,"E16"),sQuery(id+"F0.wireOp",EDGE,"E23.trimOffspring"),sQuery(id+"F0.wireOp",EDGE,"E24"),sQuery(id+"F0.wireOp",EDGE,"E25"),sQuery(id+"F0.wireOp",EDGE,"E26"),sQuery(id+"F0.wireOp",EDGE,"E27"),sQuery(id+"F0.wireOp",EDGE,"E28.1.0"),sQuery(id+"F0.wireOp",EDGE,"E28.1.1"),sQuery(id+"F0.wireOp",EDGE,"E28.1.2"),sQuery(id+"F0.wireOp",EDGE,"E28.1.4"),sQuery(id+"F0.wireOp",EDGE,"E28.1.5"),subQ1,subQ0,sQuery(id+"F0.wireOp",EDGE,"E28.1.11"),sQuery(id+"F0.wireOp",EDGE,"E28.1.13")])],"isStart":false})]});}
            var Q11;
            Q11=makeQuery(id+"F1.opExtrude","CAP_EDGE",EDGE,{"disambiguationData":[OSD([sQuery(id+"F0.wireOp",EDGE,"E28.1.10")])],"isStart":false});
            var Q12;
            {var subQ0=sQuery(id+"F0.wireOp",EDGE,"E28.1.11");var subQ1=sQuery(id+"F0.wireOp",EDGE,"E28.1.10");Q12=makeQuery(id+"F2.opFillet","BLEND_EDGE",EDGE,{"blendedFrom":[makeQuery(id+"F1.opExtrude","SWEPT_EDGE",EDGE,{"disambiguationData":[OSD([sQuery(id+"F0.wireOp",EDGE,"E4.right"),subQ1,subQ0])]}),makeQuery(id+"F1.opExtrude","CAP_FACE",FACE,{"disambiguationData":[OSD([sQuery(id+"F0.wireOp",EDGE,"E0.right"),sQuery(id+"F0.wireOp",EDGE,"E1"),sQuery(id+"F0.wireOp",EDGE,"E7"),sQuery(id+"F0.wireOp",EDGE,"E9.1.0"),sQuery(id+"F0.wireOp",EDGE,"E10"),sQuery(id+"F0.wireOp",EDGE,"E12"),sQuery(id+"F0.wireOp",EDGE,"E13"),sQuery(id+"F0.wireOp",EDGE,"E15"),sQuery(id+"F0.wireOp",EDGE,"E16"),sQuery(id+"F0.wireOp",EDGE,"E23.trimOffspring"),sQuery(id+"F0.wireOp",EDGE,"E24"),sQuery(id+"F0.wireOp",EDGE,"E25"),sQuery(id+"F0.wireOp",EDGE,"E26"),sQuery(id+"F0.wireOp",EDGE,"E27"),sQuery(id+"F0.wireOp",EDGE,"E28.1.0"),sQuery(id+"F0.wireOp",EDGE,"E28.1.1"),sQuery(id+"F0.wireOp",EDGE,"E28.1.2"),sQuery(id+"F0.wireOp",EDGE,"E28.1.4"),sQuery(id+"F0.wireOp",EDGE,"E28.1.5"),sQuery(id+"F0.wireOp",EDGE,"E28.1.8"),subQ1,subQ0,sQuery(id+"F0.wireOp",EDGE,"E28.1.13")])],"isStart":false})],"blendedInto":[makeQuery(id+"F1.opExtrude","CAP_FACE",FACE,{"disambiguationData":[OSD([sQuery(id+"F0.wireOp",EDGE,"E0.right"),sQuery(id+"F0.wireOp",EDGE,"E1"),sQuery(id+"F0.wireOp",EDGE,"E7"),sQuery(id+"F0.wireOp",EDGE,"E9.1.0"),sQuery(id+"F0.wireOp",EDGE,"E10"),sQuery(id+"F0.wireOp",EDGE,"E12"),sQuery(id+"F0.wireOp",EDGE,"E13"),sQuery(id+"F0.wireOp",EDGE,"E15"),sQuery(id+"F0.wireOp",EDGE,"E16"),sQuery(id+"F0.wireOp",EDGE,"E23.trimOffspring"),sQuery(id+"F0.wireOp",EDGE,"E24"),sQuery(id+"F0.wireOp",EDGE,"E25"),sQuery(id+"F0.wireOp",EDGE,"E26"),sQuery(id+"F0.wireOp",EDGE,"E27"),sQuery(id+"F0.wireOp",EDGE,"E28.1.0"),sQuery(id+"F0.wireOp",EDGE,"E28.1.1"),sQuery(id+"F0.wireOp",EDGE,"E28.1.2"),sQuery(id+"F0.wireOp",EDGE,"E28.1.4"),sQuery(id+"F0.wireOp",EDGE,"E28.1.5"),sQuery(id+"F0.wireOp",EDGE,"E28.1.8"),subQ1,subQ0,sQuery(id+"F0.wireOp",EDGE,"E28.1.13")])],"isStart":false})]});}
            var Q13;
            Q13=makeQuery(id+"F1.opExtrude","CAP_EDGE",EDGE,{"disambiguationData":[OSD([sQuery(id+"F0.wireOp",EDGE,"E28.1.11")])],"isStart":false});
            var Q14;
            Q14=makeQuery(id+"F1.opExtrude","CAP_EDGE",EDGE,{"disambiguationData":[OSD([sQuery(id+"F0.wireOp",EDGE,"E28.1.13")])],"isStart":false});
            var Q15;
            Q15=makeQuery(id+"F1.opExtrude","CAP_EDGE",EDGE,{"disambiguationData":[OSD([sQuery(id+"F0.wireOp",EDGE,"E28.1.0")])],"isStart":false});
            var Q16;
            {var subQ0=sQuery(id+"F0.wireOp",EDGE,"E28.1.1");var subQ1=sQuery(id+"F0.wireOp",EDGE,"E28.1.0");Q16=makeQuery(id+"F2.opFillet","BLEND_EDGE",EDGE,{"blendedFrom":[makeQuery(id+"F1.opExtrude","SWEPT_EDGE",EDGE,{"disambiguationData":[OSD([subQ1,subQ0])]}),makeQuery(id+"F1.opExtrude","CAP_FACE",FACE,{"disambiguationData":[OSD([sQuery(id+"F0.wireOp",EDGE,"E0.right"),sQuery(id+"F0.wireOp",EDGE,"E1"),sQuery(id+"F0.wireOp",EDGE,"E7"),sQuery(id+"F0.wireOp",EDGE,"E9.1.0"),sQuery(id+"F0.wireOp",EDGE,"E10"),sQuery(id+"F0.wireOp",EDGE,"E12"),sQuery(id+"F0.wireOp",EDGE,"E13"),sQuery(id+"F0.wireOp",EDGE,"E15"),sQuery(id+"F0.wireOp",EDGE,"E16"),sQuery(id+"F0.wireOp",EDGE,"E23.trimOffspring"),sQuery(id+"F0.wireOp",EDGE,"E24"),sQuery(id+"F0.wireOp",EDGE,"E25"),sQuery(id+"F0.wireOp",EDGE,"E26"),sQuery(id+"F0.wireOp",EDGE,"E27"),subQ1,subQ0,sQuery(id+"F0.wireOp",EDGE,"E28.1.2"),sQuery(id+"F0.wireOp",EDGE,"E28.1.4"),sQuery(id+"F0.wireOp",EDGE,"E28.1.5"),sQuery(id+"F0.wireOp",EDGE,"E28.1.8"),sQuery(id+"F0.wireOp",EDGE,"E28.1.10"),sQuery(id+"F0.wireOp",EDGE,"E28.1.11"),sQuery(id+"F0.wireOp",EDGE,"E28.1.13")])],"isStart":false})],"blendedInto":[makeQuery(id+"F1.opExtrude","CAP_FACE",FACE,{"disambiguationData":[OSD([sQuery(id+"F0.wireOp",EDGE,"E0.right"),sQuery(id+"F0.wireOp",EDGE,"E1"),sQuery(id+"F0.wireOp",EDGE,"E7"),sQuery(id+"F0.wireOp",EDGE,"E9.1.0"),sQuery(id+"F0.wireOp",EDGE,"E10"),sQuery(id+"F0.wireOp",EDGE,"E12"),sQuery(id+"F0.wireOp",EDGE,"E13"),sQuery(id+"F0.wireOp",EDGE,"E15"),sQuery(id+"F0.wireOp",EDGE,"E16"),sQuery(id+"F0.wireOp",EDGE,"E23.trimOffspring"),sQuery(id+"F0.wireOp",EDGE,"E24"),sQuery(id+"F0.wireOp",EDGE,"E25"),sQuery(id+"F0.wireOp",EDGE,"E26"),sQuery(id+"F0.wireOp",EDGE,"E27"),subQ1,subQ0,sQuery(id+"F0.wireOp",EDGE,"E28.1.2"),sQuery(id+"F0.wireOp",EDGE,"E28.1.4"),sQuery(id+"F0.wireOp",EDGE,"E28.1.5"),sQuery(id+"F0.wireOp",EDGE,"E28.1.8"),sQuery(id+"F0.wireOp",EDGE,"E28.1.10"),sQuery(id+"F0.wireOp",EDGE,"E28.1.11"),sQuery(id+"F0.wireOp",EDGE,"E28.1.13")])],"isStart":false})]});}
            var Q17;
            Q17=makeQuery(id+"F1.opExtrude","CAP_EDGE",EDGE,{"disambiguationData":[OSD([sQuery(id+"F0.wireOp",EDGE,"E28.1.2")])],"isStart":false});
            var Q18;
            Q18=makeQuery(id+"F1.opExtrude","CAP_EDGE",EDGE,{"disambiguationData":[OSD([sQuery(id+"F0.wireOp",EDGE,"E28.1.4")])],"isStart":false});
            var Q19;
            {var subQ0=sQuery(id+"F0.wireOp",EDGE,"E28.1.4");var subQ1=sQuery(id+"F0.wireOp",EDGE,"E23.trimOffspring");Q19=makeQuery(id+"F2.opFillet","BLEND_EDGE",EDGE,{"blendedFrom":[makeQuery(id+"F1.opExtrude","SWEPT_EDGE",EDGE,{"disambiguationData":[OSD([subQ1,subQ0])]}),makeQuery(id+"F1.opExtrude","CAP_FACE",FACE,{"disambiguationData":[OSD([sQuery(id+"F0.wireOp",EDGE,"E0.right"),sQuery(id+"F0.wireOp",EDGE,"E1"),sQuery(id+"F0.wireOp",EDGE,"E7"),sQuery(id+"F0.wireOp",EDGE,"E9.1.0"),sQuery(id+"F0.wireOp",EDGE,"E10"),sQuery(id+"F0.wireOp",EDGE,"E12"),sQuery(id+"F0.wireOp",EDGE,"E13"),sQuery(id+"F0.wireOp",EDGE,"E15"),sQuery(id+"F0.wireOp",EDGE,"E16"),subQ1,sQuery(id+"F0.wireOp",EDGE,"E24"),sQuery(id+"F0.wireOp",EDGE,"E25"),sQuery(id+"F0.wireOp",EDGE,"E26"),sQuery(id+"F0.wireOp",EDGE,"E27"),sQuery(id+"F0.wireOp",EDGE,"E28.1.0"),sQuery(id+"F0.wireOp",EDGE,"E28.1.1"),sQuery(id+"F0.wireOp",EDGE,"E28.1.2"),subQ0,sQuery(id+"F0.wireOp",EDGE,"E28.1.5"),sQuery(id+"F0.wireOp",EDGE,"E28.1.8"),sQuery(id+"F0.wireOp",EDGE,"E28.1.10"),sQuery(id+"F0.wireOp",EDGE,"E28.1.11"),sQuery(id+"F0.wireOp",EDGE,"E28.1.13")])],"isStart":false})],"blendedInto":[makeQuery(id+"F1.opExtrude","CAP_FACE",FACE,{"disambiguationData":[OSD([sQuery(id+"F0.wireOp",EDGE,"E0.right"),sQuery(id+"F0.wireOp",EDGE,"E1"),sQuery(id+"F0.wireOp",EDGE,"E7"),sQuery(id+"F0.wireOp",EDGE,"E9.1.0"),sQuery(id+"F0.wireOp",EDGE,"E10"),sQuery(id+"F0.wireOp",EDGE,"E12"),sQuery(id+"F0.wireOp",EDGE,"E13"),sQuery(id+"F0.wireOp",EDGE,"E15"),sQuery(id+"F0.wireOp",EDGE,"E16"),subQ1,sQuery(id+"F0.wireOp",EDGE,"E24"),sQuery(id+"F0.wireOp",EDGE,"E25"),sQuery(id+"F0.wireOp",EDGE,"E26"),sQuery(id+"F0.wireOp",EDGE,"E27"),sQuery(id+"F0.wireOp",EDGE,"E28.1.0"),sQuery(id+"F0.wireOp",EDGE,"E28.1.1"),sQuery(id+"F0.wireOp",EDGE,"E28.1.2"),subQ0,sQuery(id+"F0.wireOp",EDGE,"E28.1.5"),sQuery(id+"F0.wireOp",EDGE,"E28.1.8"),sQuery(id+"F0.wireOp",EDGE,"E28.1.10"),sQuery(id+"F0.wireOp",EDGE,"E28.1.11"),sQuery(id+"F0.wireOp",EDGE,"E28.1.13")])],"isStart":false})]});}
            var Q20;
            Q20=makeQuery(id+"F1.opExtrude","CAP_EDGE",EDGE,{"disambiguationData":[OSD([sQuery(id+"F0.wireOp",EDGE,"E23.trimOffspring")])],"isStart":false});
            var Q21;
            Q21=makeQuery(id+"F1.opExtrude","CAP_EDGE",EDGE,{"disambiguationData":[OSD([sQuery(id+"F0.wireOp",EDGE,"E28.1.1")])],"isStart":false});
            var Q22;
            Q22=makeQuery(id+"F2.opFillet","BLEND_FACE",FACE,{"disambiguationData":[OSD([sQuery(id+"F0.wireOp",EDGE,"E21"),sQuery(id+"F0.wireOp",EDGE,"E23.trimOffspring"),sQuery(id+"F0.wireOp",EDGE,"E27")])]});
            var Q23;
            Q23=makeQuery(id+"F1.opExtrude","CAP_EDGE",EDGE,{"disambiguationData":[OSD([sQuery(id+"F0.wireOp",EDGE,"E27")])],"isStart":false});
            var Q24;
            Q24=makeQuery(id+"F1.opExtrude","CAP_EDGE",EDGE,{"disambiguationData":[OSD([sQuery(id+"F0.wireOp",EDGE,"E15")])],"isStart":false});
            fillet(context, id + "F4", {"entities" : qUnion([Q0, Q1, Q2, Q3, Q4, Q5, Q6, Q7, Q8, Q9, Q10, Q11, Q12, Q13, Q14, Q15, Q16, Q17, Q18, Q19, Q20, Q21, Q22, Q23, Q24]), "radius" : 2 * mm, "tangentPropagation" : true, "allowEdgeOverflow" : false});
        }
        {
            var Q0;
            Q0=qCreatedBy(makeId("Top.planeOp"),FACE);
            var sketch = newSketch(context, id + "F5", { "sketchPlane" : qUnion([Q0])});
            skCircle(sketch, "E32", {"center": v(-7.88, -13.53) * mm, "radius": 2.75 * mm});
            skCircle(sketch, "E33.1.0", {"center": v(7.88, 13.53) * mm, "radius": 2.75 * mm});
            skPoint(sketch, "E33.center", {"position": v(0, 0) * mm});
            skCircle(sketch, "E34.1.0.0", {"center": v(-1.1, -15.7) * mm, "radius": 2.75 * mm});
            skCircle(sketch, "E35.1.0", {"center": v(1.1, 15.7) * mm, "radius": 2.75 * mm});
            skSolve(sketch);
        }
        {
            var Q0;
            Q0=makeQuery(id+"F5.imprint","IMPRINT",FACE,{"disambiguationData":[TD([[makeQuery(id+"F5.imprint","IMPRINT",EDGE,{"derivedFrom":sQuery(id+"F5.wireOp",EDGE,"E33.1.0")}),1.0]])]});
            var Q1;
            Q1=makeQuery(id+"F5.imprint","IMPRINT",FACE,{"disambiguationData":[TD([[makeQuery(id+"F5.imprint","IMPRINT",EDGE,{"derivedFrom":sQuery(id+"F5.wireOp",EDGE,"E35.1.0")}),1.0]])]});
            var Q2;
            Q2=makeQuery(id+"F5.imprint","IMPRINT",FACE,{"disambiguationData":[TD([[makeQuery(id+"F5.imprint","IMPRINT",EDGE,{"derivedFrom":sQuery(id+"F5.wireOp",EDGE,"E34.1.0.0")}),1.0]])]});
            var Q3;
            Q3=makeQuery(id+"F5.imprint","IMPRINT",FACE,{"disambiguationData":[TD([[makeQuery(id+"F5.imprint","IMPRINT",EDGE,{"derivedFrom":sQuery(id+"F5.wireOp",EDGE,"E32")}),1.0]])]});
            extrude(context, id + "F6", {"entities" : qUnion([Q0, Q1, Q2, Q3]), "operationType" : NewBodyOperationType.REMOVE, "depth" : 7 * mm, "offsetDistance" : 25 * mm});
        }
    });
